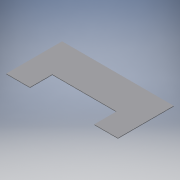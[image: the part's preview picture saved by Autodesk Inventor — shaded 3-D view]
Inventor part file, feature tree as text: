
AUTODESK INVENTOR PART (.ipt)
format: ipt  version: 2016 (Build 200138000, 138)  size: 108,544 bytes
history: native  units: mm
features: extrude x2, sketch x2
ambient origin geometry x8: Origin, YZ Plane, XZ Plane, XY Plane, X Axis, Y Axis, Z Axis, Center Point
bodies: Solid1 (feature_tree)
feature tree (4):
  extrude  "Extrusion1"  Depth=10.0mm TaperAngle=0.0deg
  extrude  "Extrusion2"  [1 undecoded]
  sketch  "Sketch1"  dims[d4=0.0mm d8=10.0mm d9=0.0mm]
  sketch  "Sketch2"  dims[d10=1100.0mm]
note: 1 required parameter value undecoded (feature->parameter linkage not recoverable at this tier; creation-order binding heuristic only, values carry confidence <= 0.55)
